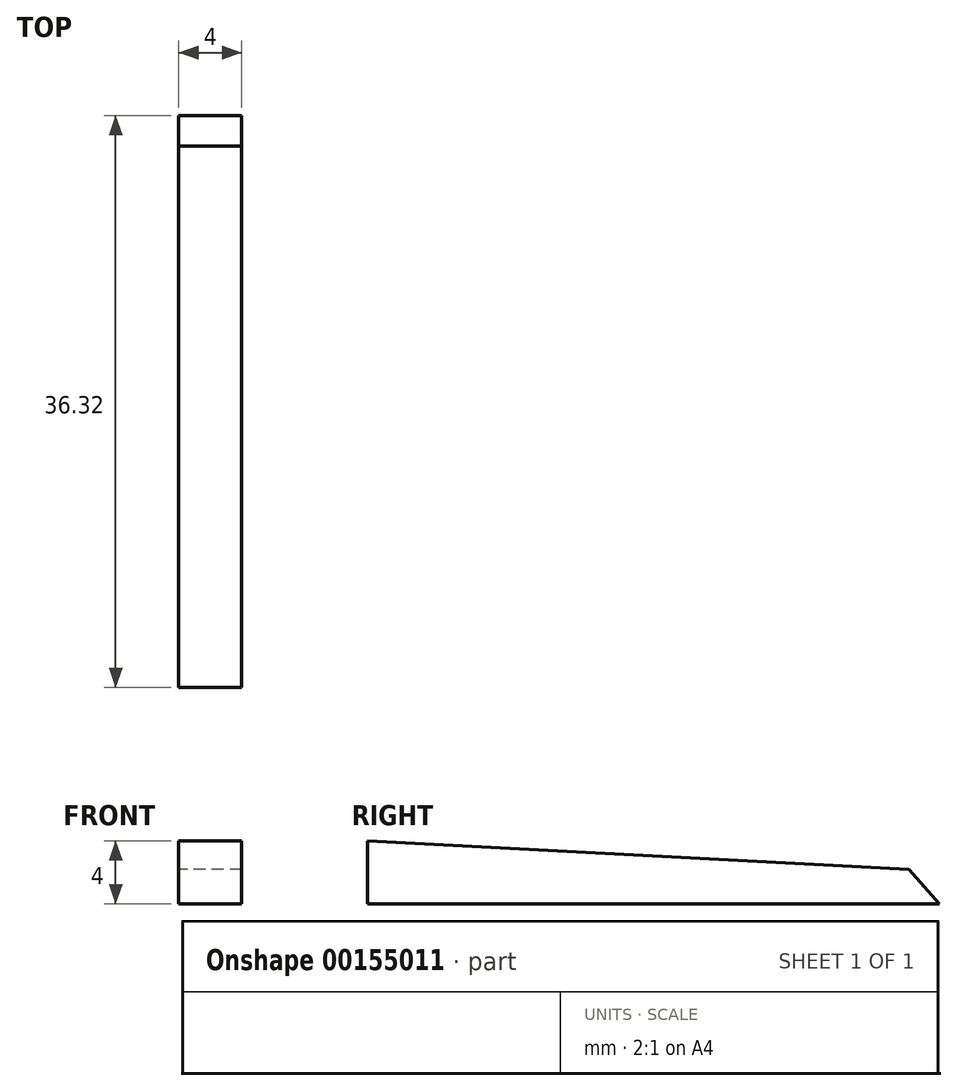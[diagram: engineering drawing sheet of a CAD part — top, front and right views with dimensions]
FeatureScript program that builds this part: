
annotation { "Feature Type Name" : "Feature", "Feature Type Description" : "" }
export const myFeature = defineFeature(function(context is Context, id is Id, definition is map)
    precondition{}
    {
        {
            var Q0;
            Q0=qCreatedBy(makeId("Right.planeOp"),FACE);
            var sketch = newSketch(context, id + "F0", { "sketchPlane" : qUnion([Q0])});
            skLineSegment(sketch, "E0", {"start": v(-41.72, 2.2) * mm, "end": v(-76.1, 4) * mm});
            skLineSegment(sketch, "E1", {"start": v(-76.1, 4) * mm, "end": v(-76.1, 0) * mm});
            skLineSegment(sketch, "E2", {"start": v(-76.1, 0) * mm, "end": v(-39.77, 0) * mm});
            skLineSegment(sketch, "E3", {"start": v(-41.72, 2.2) * mm, "end": v(-39.77, 0) * mm});
            skSolve(sketch);
        }
        {
            var Q0;
            Q0 = qSketchRegion(id + "F0", true);
            extrude(context, id + "F1", {"entities" : qUnion([Q0]), "depth" : 4 * mm});
        }
    });
